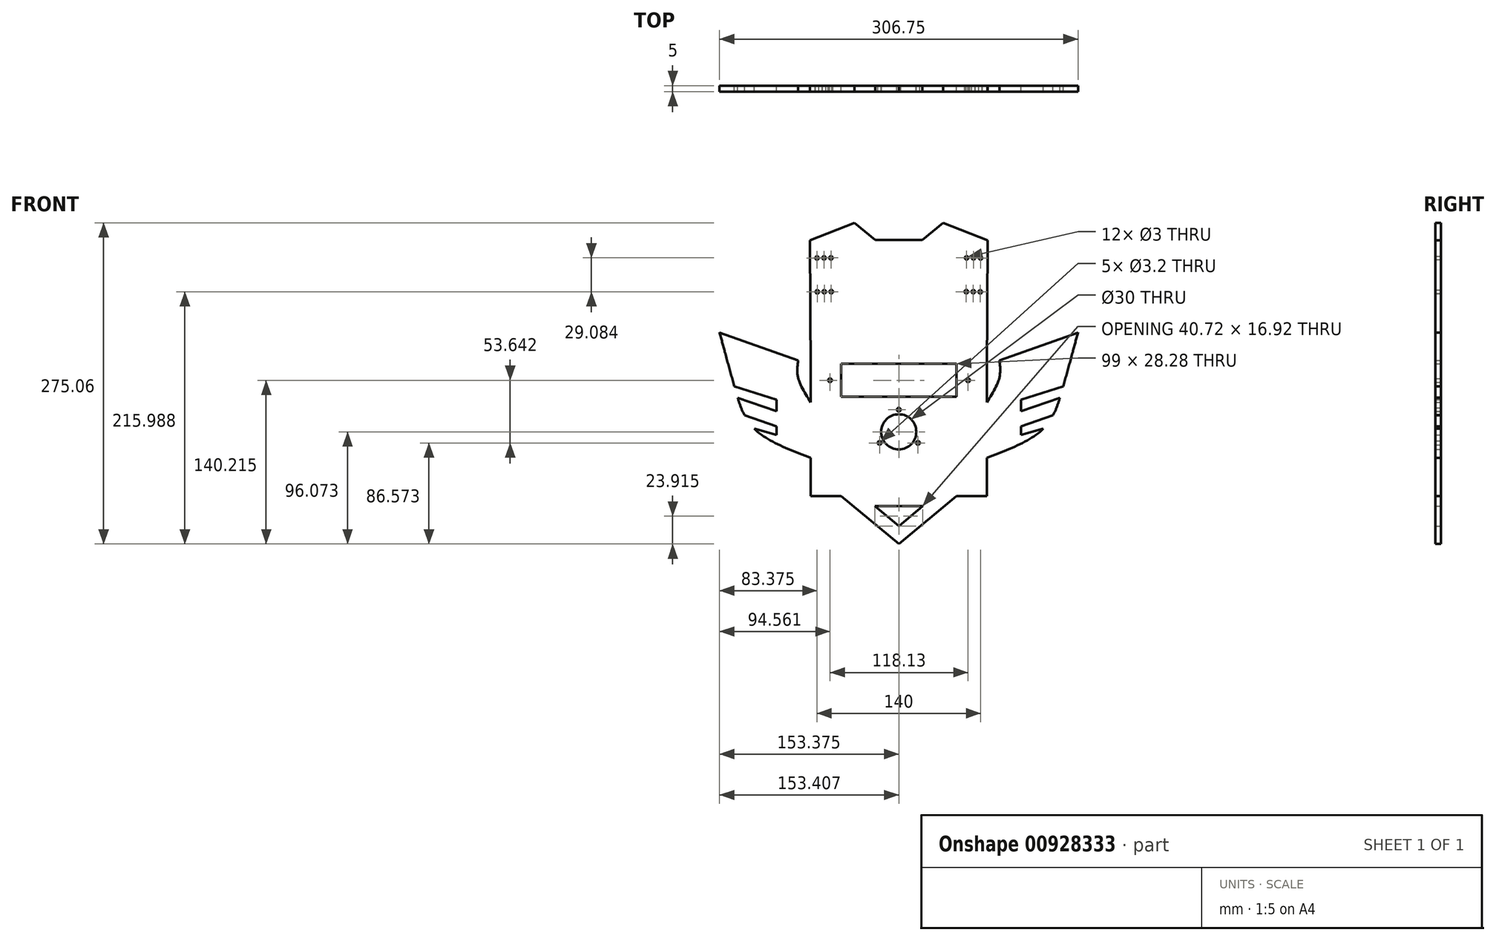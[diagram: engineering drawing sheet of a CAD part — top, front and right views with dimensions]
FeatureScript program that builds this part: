
annotation { "Feature Type Name" : "Feature", "Feature Type Description" : "" }
export const myFeature = defineFeature(function(context is Context, id is Id, definition is map)
    precondition{}
    {
        {
            var Q0;
            Q0=qCreatedBy(makeId("Front.planeOp"),FACE);
            var sketch = newSketch(context, id + "F0", { "sketchPlane" : qUnion([Q0])});
            skCircle(sketch, "E0", {"center": v(-166.9, 163.36) * mm, "radius": 1.5 * mm});
            skCircle(sketch, "E1.0.1.0", {"center": v(-166.7, 134.36) * mm, "radius": 1.5 * mm});
            skCircle(sketch, "E1.1.0.0", {"center": v(-160.9, 163.4) * mm, "radius": 1.5 * mm});
            skCircle(sketch, "E1.1.1.0", {"center": v(-160.7, 134.4) * mm, "radius": 1.5 * mm});
            skCircle(sketch, "E1.2.0.0", {"center": v(-154.9, 163.44) * mm, "radius": 1.5 * mm});
            skCircle(sketch, "E1.2.1.0", {"center": v(-154.7, 134.44) * mm, "radius": 1.5 * mm});
            skLineSegment(sketch, "E1.direction1", {"start": v(-166.9, 163.36) * mm, "end": v(-160.9, 163.4) * mm, "construction": true});
            skLineSegment(sketch, "E1.direction2", {"start": v(-166.9, 163.36) * mm, "end": v(-166.7, 134.36) * mm, "construction": true});
            skLineSegment(sketch, "E2", {"start": v(-96.9, 163.6) * mm, "end": v(-96.9, 88.6) * mm});
            skCircle(sketch, "E3.MirrorC", {"center": v(-32.9, 163.4) * mm, "radius": 1.5 * mm});
            skCircle(sketch, "E4.MirrorC", {"center": v(-39.1, 134.44) * mm, "radius": 1.5 * mm});
            skCircle(sketch, "E5.MirrorC", {"center": v(-33.1, 134.4) * mm, "radius": 1.5 * mm});
            skCircle(sketch, "E6.MirrorC", {"center": v(-27.1, 134.36) * mm, "radius": 1.5 * mm});
            skCircle(sketch, "E7.MirrorC", {"center": v(-38.9, 163.44) * mm, "radius": 1.5 * mm});
            skCircle(sketch, "E8.MirrorC", {"center": v(-26.9, 163.36) * mm, "radius": 1.5 * mm});
            skLineSegment(sketch, "E9", {"start": v(-173, 178.32) * mm, "end": v(-172.2, 64.57) * mm});
            skLineSegment(sketch, "E10", {"start": v(-173, 178.32) * mm, "end": v(-96.9, 178.85) * mm});
            skCircle(sketch, "E11", {"center": v(-96.9, 14.44) * mm, "radius": 15 * mm});
            skLineSegment(sketch, "E12", {"start": v(-172.2, 64.57) * mm, "end": v(-172.2, -40.54) * mm});
            skLineSegment(sketch, "E13", {"start": v(-172.2, -40.54) * mm, "end": v(-96.9, -40.54) * mm});
            skLineSegment(sketch, "E14.MirrorCS", {"start": v(-20.8, 178.32) * mm, "end": v(-96.9, 178.85) * mm});
            skLineSegment(sketch, "E15.MirrorCS", {"start": v(-20.8, 178.32) * mm, "end": v(-21.6, 64.57) * mm});
            skLineSegment(sketch, "E16.MirrorCS", {"start": v(-21.6, 64.57) * mm, "end": v(-21.6, -40.54) * mm});
            skLineSegment(sketch, "E17.MirrorCS", {"start": v(-21.6, -40.54) * mm, "end": v(-96.9, -40.54) * mm});
            skPoint(sketch, "E18.start.orphan", {"position": v(-172.49, 79.43) * mm});
            skLineSegment(sketch, "E19", {"start": v(-146.4, 72.73) * mm, "end": v(-160.55, 58.59) * mm});
            skLineSegment(sketch, "E20", {"start": v(-160.55, 58.59) * mm, "end": v(-146.4, 44.44) * mm});
            skLineSegment(sketch, "E21.MirrorCS", {"start": v(-47.4, 72.73) * mm, "end": v(-33.26, 58.59) * mm});
            skLineSegment(sketch, "E22.MirrorCS", {"start": v(-33.26, 58.59) * mm, "end": v(-47.4, 44.44) * mm});
            skLineSegment(sketch, "E23", {"start": v(-146.4, 72.73) * mm, "end": v(-146.4, 44.44) * mm});
            skLineSegment(sketch, "E24", {"start": v(-47.4, 72.73) * mm, "end": v(-47.4, 44.44) * mm});
            skCircle(sketch, "E25", {"center": v(-155.72, 58.59) * mm, "radius": 1.6 * mm});
            skCircle(sketch, "E26", {"center": v(-37.59, 58.59) * mm, "radius": 1.6 * mm});
            skPoint(sketch, "E27.end.orphan", {"position": v(-97.03, 44.44) * mm});
            skLineSegment(sketch, "E28", {"start": v(-146.4, 44.44) * mm, "end": v(-47.4, 44.44) * mm});
            skPoint(sketch, "E29.start.orphan", {"position": v(-96.9, 83.87) * mm});
            skLineSegment(sketch, "E30", {"start": v(-146.4, 72.73) * mm, "end": v(-47.4, 72.73) * mm});
            skPoint(sketch, "E31.start.orphan", {"position": v(-21.32, 104.4) * mm});
            skLineSegment(sketch, "E32.MirrorCS", {"start": v(-250.28, 99.51) * mm, "end": v(-183.04, 75.67) * mm});
            skFitSpline(sketch, "E33.MirrorCS", {"points": [v(-183.04, 75.67) * mm, v(-183.04, 60.94) * mm, v(-172.2, 39.6) * mm], "startDerivative": vector(-4.25, -32.5) * mm, "endDerivative": vector(24.75, -39.36) * mm});
            skFitSpline(sketch, "E34.MirrorCS", {"points": [v(-250.58, 100.64) * mm, v(-236.66, 49.88) * mm, v(-220.7, 17.14) * mm, v(-172.2, -7.83) * mm], "startDerivative": vector(40.58, -151.25) * mm, "endDerivative": vector(158.27, -59.78) * mm});
            skLineSegment(sketch, "E35.MirrorCS", {"start": v(-245.83, 82.95) * mm, "end": v(-198.52, 66.78) * mm});
            skLineSegment(sketch, "E36.MirrorCS", {"start": v(-198.52, 56.78) * mm, "end": v(-241.44, 70.29) * mm});
            skLineSegment(sketch, "E37.MirrorCS", {"start": v(-198.52, 66.78) * mm, "end": v(-198.52, 56.78) * mm});
            skLineSegment(sketch, "E38.MirrorCS", {"start": v(-237.7, 53.5) * mm, "end": v(-201.45, 42.1) * mm});
            skLineSegment(sketch, "E39.MirrorCS", {"start": v(-201.45, 32.1) * mm, "end": v(-234.78, 43.5) * mm});
            skPoint(sketch, "E40.MirrorP", {"position": v(-198.52, 41.16) * mm});
            skLineSegment(sketch, "E41.MirrorCS", {"start": v(-201.45, 42.1) * mm, "end": v(-201.45, 32.1) * mm});
            skLineSegment(sketch, "E42.MirrorCS", {"start": v(-228.96, 28.55) * mm, "end": v(-201.45, 19.14) * mm});
            skLineSegment(sketch, "E43.MirrorCS", {"start": v(-201.45, 11.85) * mm, "end": v(-220.7, 17.14) * mm});
            skLineSegment(sketch, "E44.MirrorCS", {"start": v(-201.45, 19.14) * mm, "end": v(-201.45, 11.85) * mm});
            skPoint(sketch, "E45.2.internal.snap0", {"position": v(-59.25, -40.54) * mm});
            skPoint(sketch, "E45.2.internal.orphan", {"position": v(-59.25, -83.4) * mm});
            skLineSegment(sketch, "E46", {"start": v(-146.4, -40.54) * mm, "end": v(-96.9, -81.63) * mm});
            skLineSegment(sketch, "E47", {"start": v(-96.9, -81.63) * mm, "end": v(-47.4, -40.54) * mm});
            skPoint(sketch, "E48.orphan", {"position": v(-253.44, 100.64) * mm});
            skLineSegment(sketch, "E49.MirrorCS", {"start": v(4.7, 66.78) * mm, "end": v(4.7, 56.78) * mm});
            skLineSegment(sketch, "E50.MirrorCS", {"start": v(7.64, 19.14) * mm, "end": v(7.64, 11.85) * mm});
            skLineSegment(sketch, "E51.MirrorCS", {"start": v(7.64, 42.1) * mm, "end": v(7.64, 32.1) * mm});
            skLineSegment(sketch, "E52.MirrorCS", {"start": v(52.02, 82.95) * mm, "end": v(4.7, 66.78) * mm});
            skLineSegment(sketch, "E53.MirrorCS", {"start": v(4.7, 56.78) * mm, "end": v(47.63, 70.29) * mm});
            skLineSegment(sketch, "E54.MirrorCS", {"start": v(43.89, 53.5) * mm, "end": v(7.64, 42.1) * mm});
            skLineSegment(sketch, "E55.MirrorCS", {"start": v(56.47, 99.51) * mm, "end": v(-10.77, 75.67) * mm});
            skLineSegment(sketch, "E56.MirrorCS", {"start": v(7.64, 11.85) * mm, "end": v(26.9, 17.14) * mm});
            skPoint(sketch, "E57.MirrorP", {"position": v(-21.32, 79.43) * mm});
            skPoint(sketch, "E58.MirrorP", {"position": v(4.7, 41.16) * mm});
            skPoint(sketch, "E59.MirrorP", {"position": v(59.63, 100.64) * mm});
            skLineSegment(sketch, "E60.MirrorCS", {"start": v(7.64, 32.1) * mm, "end": v(40.97, 43.5) * mm});
            skLineSegment(sketch, "E61.MirrorCS", {"start": v(35.15, 28.55) * mm, "end": v(7.64, 19.14) * mm});
            skFitSpline(sketch, "E62.MirrorCS", {"points": [v(56.77, 100.64) * mm, v(42.85, 49.88) * mm, v(26.9, 17.14) * mm, v(-21.6, -7.83) * mm], "startDerivative": vector(-40.58, -151.25) * mm, "endDerivative": vector(-158.27, -59.78) * mm});
            skFitSpline(sketch, "E63.MirrorCS", {"points": [v(-10.77, 75.67) * mm, v(-10.77, 60.94) * mm, v(-21.6, 39.6) * mm], "startDerivative": vector(4.25, -32.5) * mm, "endDerivative": vector(-24.75, -39.36) * mm});
            skLineSegment(sketch, "E64", {"start": v(-173, 178.32) * mm, "end": v(-134.96, 193.43) * mm});
            skPoint(sketch, "E64.endSnap0", {"position": v(-134.96, 178.58) * mm});
            skLineSegment(sketch, "E65.MirrorCS", {"start": v(-20.8, 178.32) * mm, "end": v(-58.85, 193.43) * mm});
            skPoint(sketch, "E66.MirrorCS.end.orphan", {"position": v(-96.9, 178.85) * mm});
            skPoint(sketch, "E66.MirrorCS.start.orphan", {"position": v(-58.85, 193.43) * mm});
            skLineSegment(sketch, "E67", {"start": v(-134.96, 193.43) * mm, "end": v(-116.93, 178.71) * mm});
            skLineSegment(sketch, "E68.MirrorCS", {"start": v(-58.85, 193.43) * mm, "end": v(-76.88, 178.71) * mm});
            skLineSegment(sketch, "E69", {"start": v(-117.23, -49.25) * mm, "end": v(-76.51, -49.25) * mm});
            skLineSegment(sketch, "E70", {"start": v(-76.51, -49.25) * mm, "end": v(-96.9, -66.18) * mm});
            skLineSegment(sketch, "E71", {"start": v(-96.9, -66.18) * mm, "end": v(-117.23, -49.25) * mm});
            skCircle(sketch, "E72", {"center": v(-96.9, 33.44) * mm, "radius": 1.6 * mm});
            skCircle(sketch, "E73.1.0", {"center": v(-113.36, 4.94) * mm, "radius": 1.6 * mm});
            skCircle(sketch, "E73.2.0", {"center": v(-80.45, 4.94) * mm, "radius": 1.6 * mm});
            skSolve(sketch);
        }
        {
            var Q0;
            {var subQ3=sQuery(id+"F0.wireOp",EDGE,"E46");Q0=makeQuery(id+"F0.imprint","IMPRINT",FACE,{"disambiguationData":[TD([[makeQuery(id+"F0.imprint","IMPRINT",EDGE,{"derivedFrom":subQ3}),1.0]])]});}
            var Q1;
            Q1=makeQuery(id+"F0.imprint","IMPRINT",FACE,{"disambiguationData":[TD([[makeQuery(id+"F0.imprint","IMPRINT",EDGE,{"derivedFrom":sQuery(id+"F0.wireOp",EDGE,"E0")}),-1.0]])]});
            var Q2;
            Q2=makeQuery(id+"F0.imprint","IMPRINT",FACE,{"disambiguationData":[TD([[makeQuery(id+"F0.imprint","IMPRINT",EDGE,{"derivedFrom":sQuery(id+"F0.wireOp",EDGE,"E50.MirrorCS")}),-1.0]])]});
            var Q3;
            {var subQ6=sQuery(id+"F0.wireOp",EDGE,"E32.MirrorCS");Q3=makeQuery(id+"F0.imprint","IMPRINT",FACE,{"disambiguationData":[TD([[makeQuery(id+"F0.imprint","IMPRINT",EDGE,{"derivedFrom":subQ6}),-1.0]])]});}
            var Q4;
            Q4=makeQuery(id+"F0.imprint","IMPRINT",FACE,{"disambiguationData":[TD([[makeQuery(id+"F0.imprint","IMPRINT",EDGE,{"derivedFrom":sQuery(id+"F0.wireOp",EDGE,"E19")}),1.0]])]});
            var Q5;
            Q5=makeQuery(id+"F0.imprint","IMPRINT",FACE,{"disambiguationData":[TD([[makeQuery(id+"F0.imprint","IMPRINT",EDGE,{"derivedFrom":sQuery(id+"F0.wireOp",EDGE,"E21.MirrorCS")}),-1.0]])]});
            var Q6;
            {var subQ0=sQuery(id+"F0.wireOp",EDGE,"E64");Q6=makeQuery(id+"F0.imprint","IMPRINT",FACE,{"disambiguationData":[TD([[makeQuery(id+"F0.imprint","IMPRINT",EDGE,{"derivedFrom":subQ0}),-1.0]])]});}
            var Q7;
            {var subQ0=sQuery(id+"F0.wireOp",EDGE,"E65.MirrorCS");Q7=makeQuery(id+"F0.imprint","IMPRINT",FACE,{"disambiguationData":[TD([[makeQuery(id+"F0.imprint","IMPRINT",EDGE,{"derivedFrom":subQ0}),1.0]])]});}
            extrude(context, id + "F1", {"entities" : qUnion([Q0, Q1, Q2, Q3, Q4, Q5, Q6, Q7]), "depth" : 5 * mm, "offsetDistance" : 25 * mm});
        }
    });
